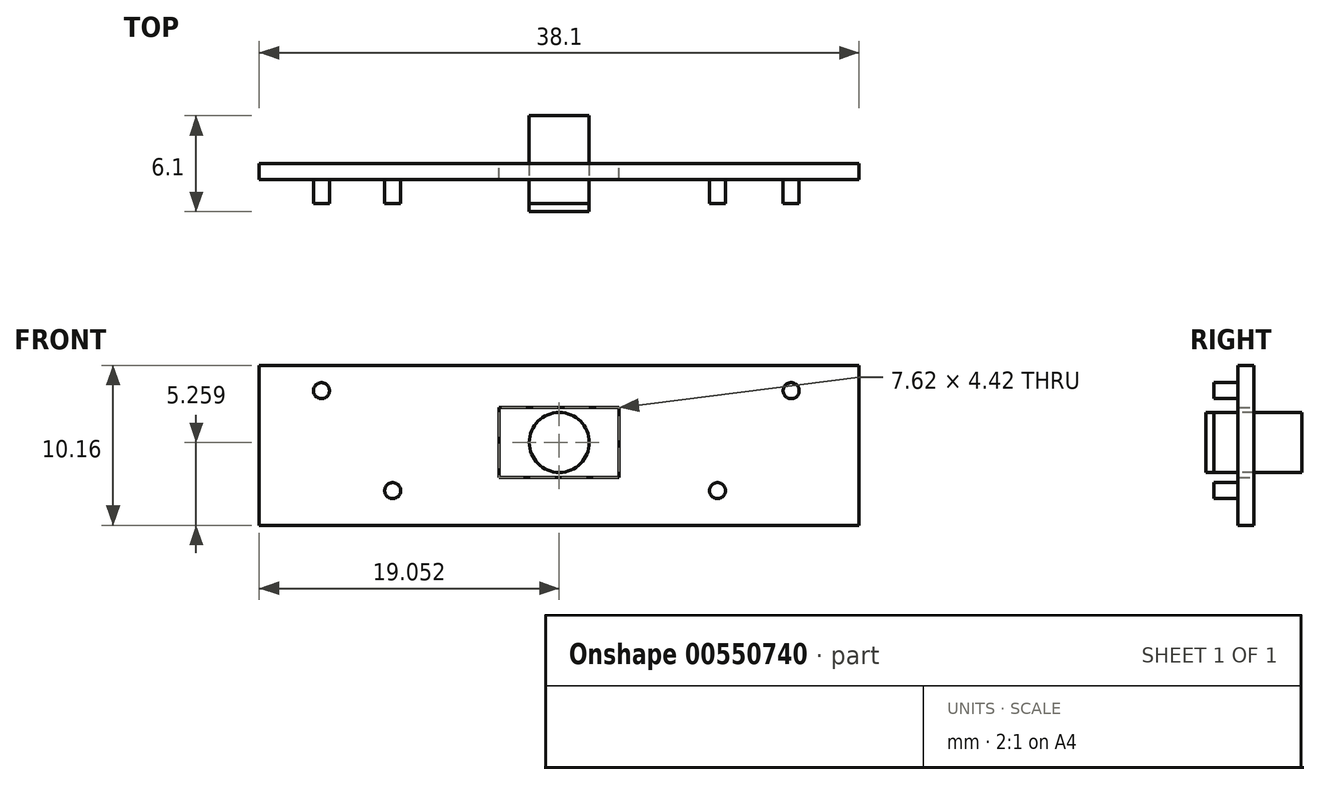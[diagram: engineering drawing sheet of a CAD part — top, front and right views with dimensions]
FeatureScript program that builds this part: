
annotation { "Feature Type Name" : "Feature", "Feature Type Description" : "" }
export const myFeature = defineFeature(function(context is Context, id is Id, definition is map)
    precondition{}
    {
        {
            var Q0;
            Q0=qCreatedBy(makeId("Front.planeOp"),FACE);
            var sketch = newSketch(context, id + "F0", { "sketchPlane" : qUnion([Q0])});
            skLineSegment(sketch, "E0.bottom", {"start": v(-30.49, 13.84) * mm, "end": v(7.61, 13.84) * mm});
            skLineSegment(sketch, "E0.top", {"start": v(-30.49, 3.68) * mm, "end": v(7.61, 3.68) * mm});
            skLineSegment(sketch, "E0.left", {"start": v(-30.49, 13.84) * mm, "end": v(-30.49, 3.68) * mm});
            skLineSegment(sketch, "E0.right", {"start": v(7.61, 13.84) * mm, "end": v(7.61, 3.68) * mm});
            skSolve(sketch);
        }
        {
            var Q0;
            Q0 = qSketchRegion(id + "F0", true);
            extrude(context, id + "F1", {"entities" : qUnion([Q0]), "depth" : 1.02 * mm, "offsetDistance" : 25.4 * mm});
        }
        {
            var Q0;
            Q0=qCreatedBy(makeId("Front.planeOp"),FACE);
            var sketch = newSketch(context, id + "F2", { "sketchPlane" : qUnion([Q0])});
            skCircle(sketch, "E1", {"center": v(3.29, 12.22) * mm, "radius": 0.5 * mm});
            skCircle(sketch, "E2", {"center": v(-1.4, 5.88) * mm, "radius": 0.5 * mm});
            skCircle(sketch, "E3", {"center": v(-26.54, 12.22) * mm, "radius": 0.5 * mm});
            skCircle(sketch, "E4", {"center": v(-22.02, 5.88) * mm, "radius": 0.5 * mm});
            skSolve(sketch);
        }
        {
            var Q0;
            Q0 = qSketchRegion(id + "F2", true);
            extrude(context, id + "F3", {"entities" : qUnion([Q0]), "operationType" : NewBodyOperationType.ADD, "depth" : 2.54 * mm, "offsetDistance" : 25.4 * mm});
        }
        {
            var Q0;
            Q0=qCreatedBy(makeId("Front.planeOp"),FACE);
            var sketch = newSketch(context, id + "F4", { "sketchPlane" : qUnion([Q0])});
            skLineSegment(sketch, "E5.bottom", {"start": v(-15.25, 11.15) * mm, "end": v(-7.63, 11.15) * mm});
            skLineSegment(sketch, "E5.top", {"start": v(-15.25, 6.73) * mm, "end": v(-7.63, 6.73) * mm});
            skLineSegment(sketch, "E5.left", {"start": v(-15.25, 11.15) * mm, "end": v(-15.25, 6.73) * mm});
            skLineSegment(sketch, "E5.right", {"start": v(-7.63, 11.15) * mm, "end": v(-7.63, 6.73) * mm});
            skSolve(sketch);
        }
        {
            var Q0;
            Q0 = qSketchRegion(id + "F4", true);
            extrude(context, id + "F5", {"entities" : qUnion([Q0]), "operationType" : NewBodyOperationType.REMOVE, "depth" : 2.54 * mm, "offsetDistance" : 25.4 * mm});
        }
        {
            var Q0;
            Q0=qCreatedBy(makeId("Front.planeOp"),FACE);
            var sketch = newSketch(context, id + "F6", { "sketchPlane" : qUnion([Q0])});
            skCircle(sketch, "E6", {"center": v(-11.44, 8.94) * mm, "radius": 1.9 * mm});
            skSolve(sketch);
        }
        {
            var Q0;
            Q0 = qSketchRegion(id + "F6", true);
            extrude(context, id + "F7", {"entities" : qUnion([Q0]), "oppositeDirection" : true, "depth" : 3.05 * mm, "offsetDistance" : 25.4 * mm, "hasSecondDirection" : true, "secondDirectionOppositeDirection" : false, "secondDirectionDepth" : 3.05 * mm});
        }
    });
